SOLIDWORKS PART (.sldprt)
format: sldprt  version: not decoded by parser v0  size: 295,936 bytes
history: native  units: mm
features: sketch x7, cut_extrude x5, material x1, extrude x1 (+13 scaffold rows collapsed)
feature tree (27):
  scaffold x13  (default folders/planes/origin — collapsed)
  material  "Material <not specified>"
  sketch  "Sketch1"  dims[D1=0.0mm]
  extrude  "Boss-Extrude1"  Depth=3mm
  sketch  "Sketch3"
  sketch  "Sketch4"
  cut_extrude  "Cut-Extrude1"  [1 undecoded]
  sketch  "Sketch5"  dims[D1=0.0mm D2=0.0mm]
  cut_extrude  "Cut-Extrude2"  [1 undecoded]
  sketch  "Sketch6"  dims[D1=0.0mm]
  cut_extrude  "Cut-Extrude3"  [1 undecoded]
  sketch  "Sketch7"  dims[D1=6.0mm]
  cut_extrude  "Cut-Extrude4"  [1 undecoded]
  sketch  "Sketch8"
  cut_extrude  "Cut-Extrude5"  [1 undecoded]
decode coverage: 5 of 13 modeling features carry decoded parameters
note: 5 parameter values undecoded
summary: no parameter record found for 5 features
note: suppression state not decoded; provenance and decode notes live in map.json
